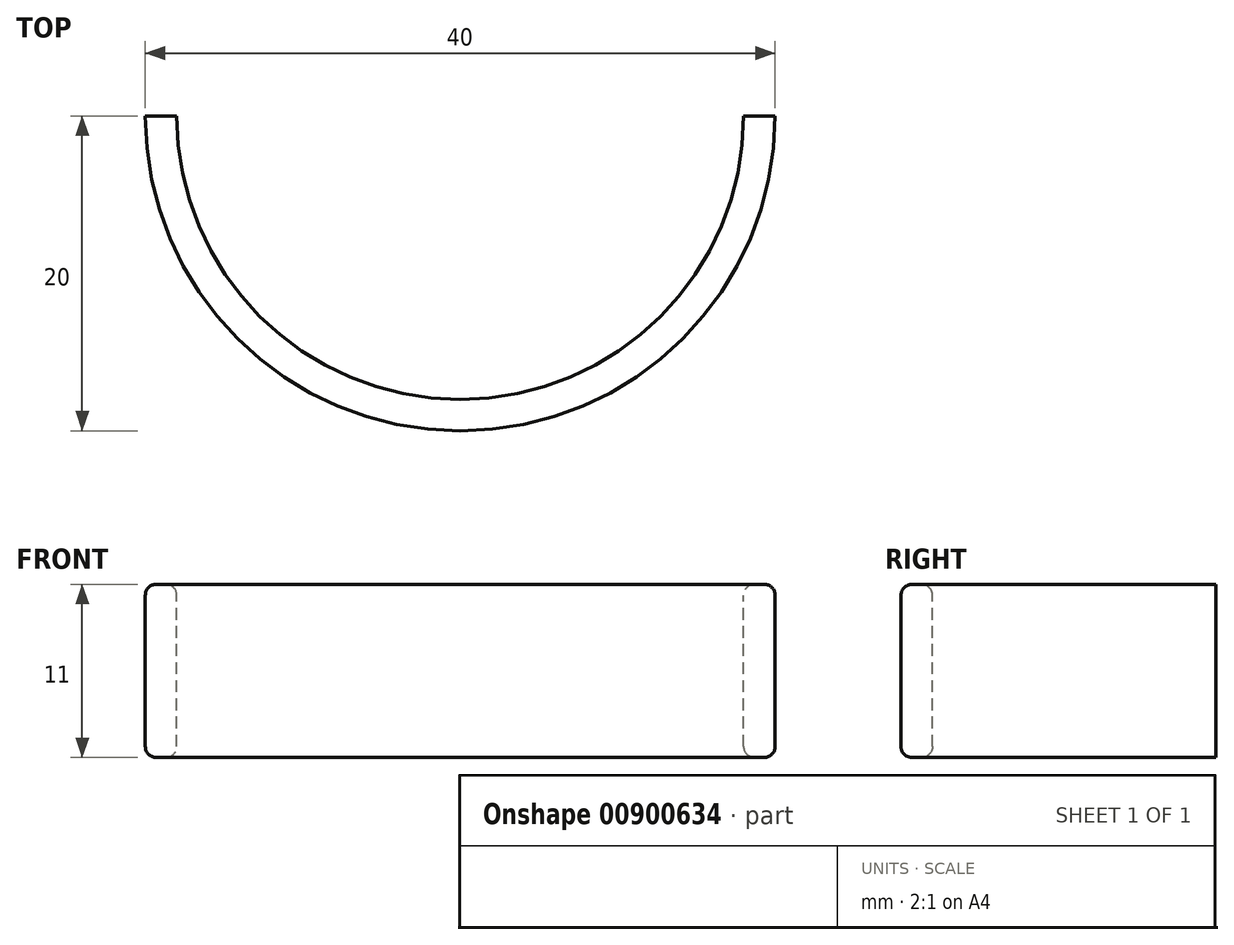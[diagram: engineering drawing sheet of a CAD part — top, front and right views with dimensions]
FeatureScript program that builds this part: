
annotation { "Feature Type Name" : "Feature", "Feature Type Description" : "" }
export const myFeature = defineFeature(function(context is Context, id is Id, definition is map)
    precondition{}
    {
        {
            var Q0;
            Q0=qCreatedBy(makeId("Front.planeOp"),FACE);
            var sketch = newSketch(context, id + "F0", { "sketchPlane" : qUnion([Q0])});
            skLineSegment(sketch, "E0.bottom", {"start": v(17.68, 1.96) * mm, "end": v(19.68, 1.96) * mm});
            skLineSegment(sketch, "E0.top", {"start": v(17.68, -9.04) * mm, "end": v(19.68, -9.04) * mm});
            skLineSegment(sketch, "E0.left", {"start": v(17.68, 1.96) * mm, "end": v(17.68, -9.04) * mm});
            skLineSegment(sketch, "E0.right", {"start": v(19.68, 1.96) * mm, "end": v(19.68, -9.04) * mm});
            skLineSegment(sketch, "E1", {"start": v(-0.32, 9.56) * mm, "end": v(-0.32, -12.19) * mm, "construction": true});
            skSolve(sketch);
        }
        {
            var Q0;
            Q0=makeQuery(id+"F0.imprint","IMPRINT",FACE,{"disambiguationData":[TD([[makeQuery(id+"F0.imprint","IMPRINT",EDGE,{"derivedFrom":sQuery(id+"F0.wireOp",EDGE,"E0.bottom")}),-1.0]])]});
            var Q1;
            Q1=sQuery(id+"F0.wireOp",EDGE,"E1");
            revolve(context, id + "F1", {"surfaceOperationType" : NewSurfaceOperationType.NEW, "entities" : qUnion([Q0]), "axis" : qUnion([Q1]), "revolveType" : RevolveType.FULL});
        }
        {
            var Q0;
            Q0=qCreatedBy(makeId("Front.planeOp"),FACE);
            var sketch = newSketch(context, id + "F2", { "sketchPlane" : qUnion([Q0])});
            skLineSegment(sketch, "E2.bottom", {"start": v(-68.98, 28.7) * mm, "end": v(29.89, 28.7) * mm});
            skLineSegment(sketch, "E2.top", {"start": v(-68.98, -33.84) * mm, "end": v(29.89, -33.84) * mm});
            skLineSegment(sketch, "E2.left", {"start": v(-68.98, 28.7) * mm, "end": v(-68.98, -33.84) * mm});
            skLineSegment(sketch, "E2.right", {"start": v(29.89, 28.7) * mm, "end": v(29.89, -33.84) * mm});
            skSolve(sketch);
        }
        {
            var Q0;
            Q0=makeQuery(id+"F2.imprint","IMPRINT",FACE,{"disambiguationData":[TD([[makeQuery(id+"F2.imprint","IMPRINT",EDGE,{"derivedFrom":sQuery(id+"F2.wireOp",EDGE,"E2.bottom")}),-1.0]])]});
            extrude(context, id + "F3", {"entities" : qUnion([Q0]), "operationType" : NewBodyOperationType.REMOVE, "endBound" : BoundingType.THROUGH_ALL, "oppositeDirection" : true, "depth" : 25 * mm, "offsetDistance" : 25 * mm});
        }
        {
            var Q0;
            Q0=makeQuery(id+"F1.opRevolve","SWEPT_EDGE",EDGE,{"disambiguationData":[OSD([sQuery(id+"F0.wireOp",EDGE,"E0.bottom"),sQuery(id+"F0.wireOp",EDGE,"E0.right")])]});
            var Q1;
            Q1=makeQuery(id+"F1.opRevolve","SWEPT_EDGE",EDGE,{"disambiguationData":[OSD([sQuery(id+"F0.wireOp",EDGE,"E0.bottom"),sQuery(id+"F0.wireOp",EDGE,"E0.left")])]});
            var Q2;
            Q2=makeQuery(id+"F1.opRevolve","SWEPT_EDGE",EDGE,{"disambiguationData":[OSD([sQuery(id+"F0.wireOp",EDGE,"E0.top"),sQuery(id+"F0.wireOp",EDGE,"E0.right")])]});
            var Q3;
            Q3=makeQuery(id+"F1.opRevolve","SWEPT_EDGE",EDGE,{"disambiguationData":[OSD([sQuery(id+"F0.wireOp",EDGE,"E0.top"),sQuery(id+"F0.wireOp",EDGE,"E0.left")])]});
            fillet(context, id + "F4", {"entities" : qUnion([Q0, Q1, Q2, Q3]), "radius" : 0.7 * mm, "tangentPropagation" : true, "allowEdgeOverflow" : false});
        }
    });
